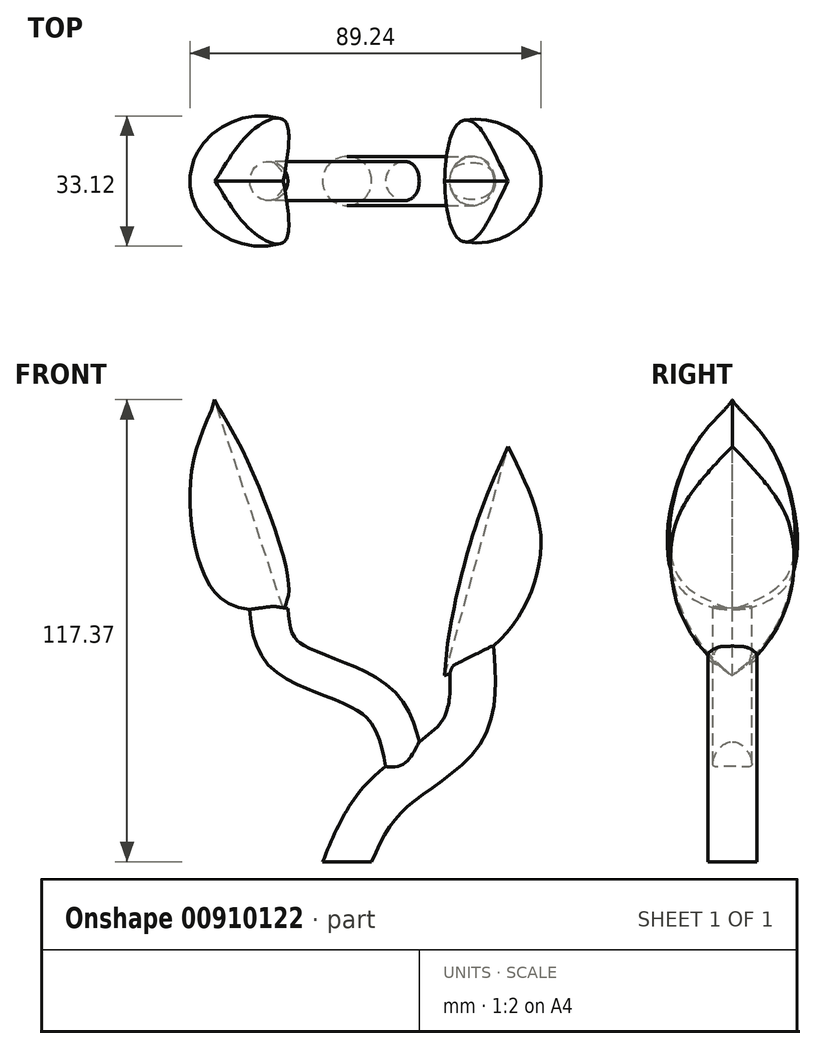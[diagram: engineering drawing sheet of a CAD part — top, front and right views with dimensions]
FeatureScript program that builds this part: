
annotation { "Feature Type Name" : "Feature", "Feature Type Description" : "" }
export const myFeature = defineFeature(function(context is Context, id is Id, definition is map)
    precondition{}
    {
        {
            var Q0;
            Q0=qCreatedBy(makeId("Front.planeOp"),FACE);
            var sketch = newSketch(context, id + "F0", { "sketchPlane" : qUnion([Q0])});
            skFitSpline(sketch, "E0", {"points": [v(0, 0) * mm, v(10.4, 17.09) * mm, v(28.86, 33.02) * mm, v(31.63, 52.19) * mm], "startDerivative": vector(24.2, 55.93) * mm, "endDerivative": vector(-3.48, 64.65) * mm});
            skSolve(sketch);
        }
        {
            var Q0;
            Q0=qCreatedBy(makeId("Top.planeOp"),FACE);
            var sketch = newSketch(context, id + "F1", { "sketchPlane" : qUnion([Q0])});
            skCircle(sketch, "E1", {"center": v(0, 0) * mm, "radius": 6.24 * mm});
            skSolve(sketch);
        }
        {
            var Q0;
            Q0=makeQuery(id+"F1.imprint","IMPRINT",FACE,{"disambiguationData":[TD([[makeQuery(id+"F1.imprint","IMPRINT",EDGE,{"derivedFrom":sQuery(id+"F1.wireOp",EDGE,"E1")}),1.0]])]});
            var Q1;
            Q1=sQuery(id+"F0.wireOp",EDGE,"E0");
            sweep(context, id + "F2", {"profiles" : qUnion([Q0]), "path" : qUnion([Q1])});
        }
        {
            var Q0;
            Q0=qCreatedBy(makeId("Front.planeOp"),FACE);
            var sketch = newSketch(context, id + "F3", { "sketchPlane" : qUnion([Q0])});
            skLineSegment(sketch, "E2", {"start": v(24.79, 47.3) * mm, "end": v(40.92, 105.52) * mm});
            skFitSpline(sketch, "E3", {"points": [v(40.92, 105.52) * mm, v(48.84, 75.86) * mm, v(24.79, 47.3) * mm], "startDerivative": vector(45.69, -91.6) * mm, "endDerivative": vector(-91.35, -34.44) * mm});
            skSolve(sketch);
        }
        {
            var Q0;
            Q0=makeQuery(id+"F3.imprint","IMPRINT",FACE,{"disambiguationData":[TD([[makeQuery(id+"F3.imprint","IMPRINT",EDGE,{"derivedFrom":sQuery(id+"F3.wireOp",EDGE,"E2")}),-1.0]])]});
            var Q1;
            Q1=sQuery(id+"F3.wireOp",EDGE,"E2");
            revolve(context, id + "F4", {"operationType" : NewBodyOperationType.ADD, "surfaceOperationType" : NewSurfaceOperationType.NEW, "entities" : qUnion([Q0]), "axis" : qUnion([Q1]), "revolveType" : RevolveType.SYMMETRIC, "angle" : 200 * degree});
        }
        {
            var Q0;
            Q0=qCreatedBy(makeId("Top.planeOp"),FACE);
            cPlane(context, id + "F5", {"entities" : qUnion([Q0]), "cplaneType" : CPlaneType.OFFSET, "offset" : 22.86 * mm, "width" : 152.4 * mm, "height" : 152.4 * mm});
        }
        {
            var Q0;
            Q0=qCreatedBy(id+"F5.planeOp",FACE);
            var sketch = newSketch(context, id + "F6", { "sketchPlane" : qUnion([Q0])});
            skCircle(sketch, "E4", {"center": v(15, 0) * mm, "radius": 4.96 * mm});
            skSolve(sketch);
        }
        {
            var Q0;
            Q0=qCreatedBy(makeId("Front.planeOp"),FACE);
            var sketch = newSketch(context, id + "F7", { "sketchPlane" : qUnion([Q0])});
            skFitSpline(sketch, "E5", {"points": [v(14.65, 22.86) * mm, v(7.7, 40.12) * mm, v(-15.76, 52.15) * mm, v(-20.3, 65.15) * mm], "startDerivative": vector(-11.28, 49.13) * mm, "endDerivative": vector(-3.58, 49.05) * mm});
            skSolve(sketch);
        }
        {
            var Q0;
            Q0=makeQuery(id+"F6.imprint","IMPRINT",FACE,{"disambiguationData":[TD([[makeQuery(id+"F6.imprint","IMPRINT",EDGE,{"derivedFrom":sQuery(id+"F6.wireOp",EDGE,"E4")}),1.0]])]});
            var Q1;
            Q1=sQuery(id+"F7.wireOp",EDGE,"E5");
            sweep(context, id + "F8", {"operationType" : NewBodyOperationType.ADD, "profiles" : qUnion([Q0]), "path" : qUnion([Q1])});
        }
        {
            var Q0;
            Q0=qCreatedBy(makeId("Front.planeOp"),FACE);
            var sketch = newSketch(context, id + "F9", { "sketchPlane" : qUnion([Q0])});
            skLineSegment(sketch, "E6", {"start": v(-16.12, 63.94) * mm, "end": v(-33.7, 117.37) * mm});
            skFitSpline(sketch, "E7", {"points": [v(-33.7, 117.37) * mm, v(-39.2, 100.87) * mm, v(-32.84, 67.58) * mm, v(-16.12, 63.94) * mm], "startDerivative": vector(-4.18, -30.86) * mm, "endDerivative": vector(61.96, 0.43) * mm});
            skSolve(sketch);
        }
        {
            var Q0;
            Q0=makeQuery(id+"F9.imprint","IMPRINT",FACE,{"disambiguationData":[TD([[makeQuery(id+"F9.imprint","IMPRINT",EDGE,{"derivedFrom":sQuery(id+"F9.wireOp",EDGE,"E6")}),1.0]])]});
            var Q1;
            Q1=sQuery(id+"F9.wireOp",EDGE,"E6");
            revolve(context, id + "F10", {"operationType" : NewBodyOperationType.ADD, "surfaceOperationType" : NewSurfaceOperationType.NEW, "entities" : qUnion([Q0]), "axis" : qUnion([Q1]), "revolveType" : RevolveType.SYMMETRIC, "angle" : 210 * degree});
        }
    });
